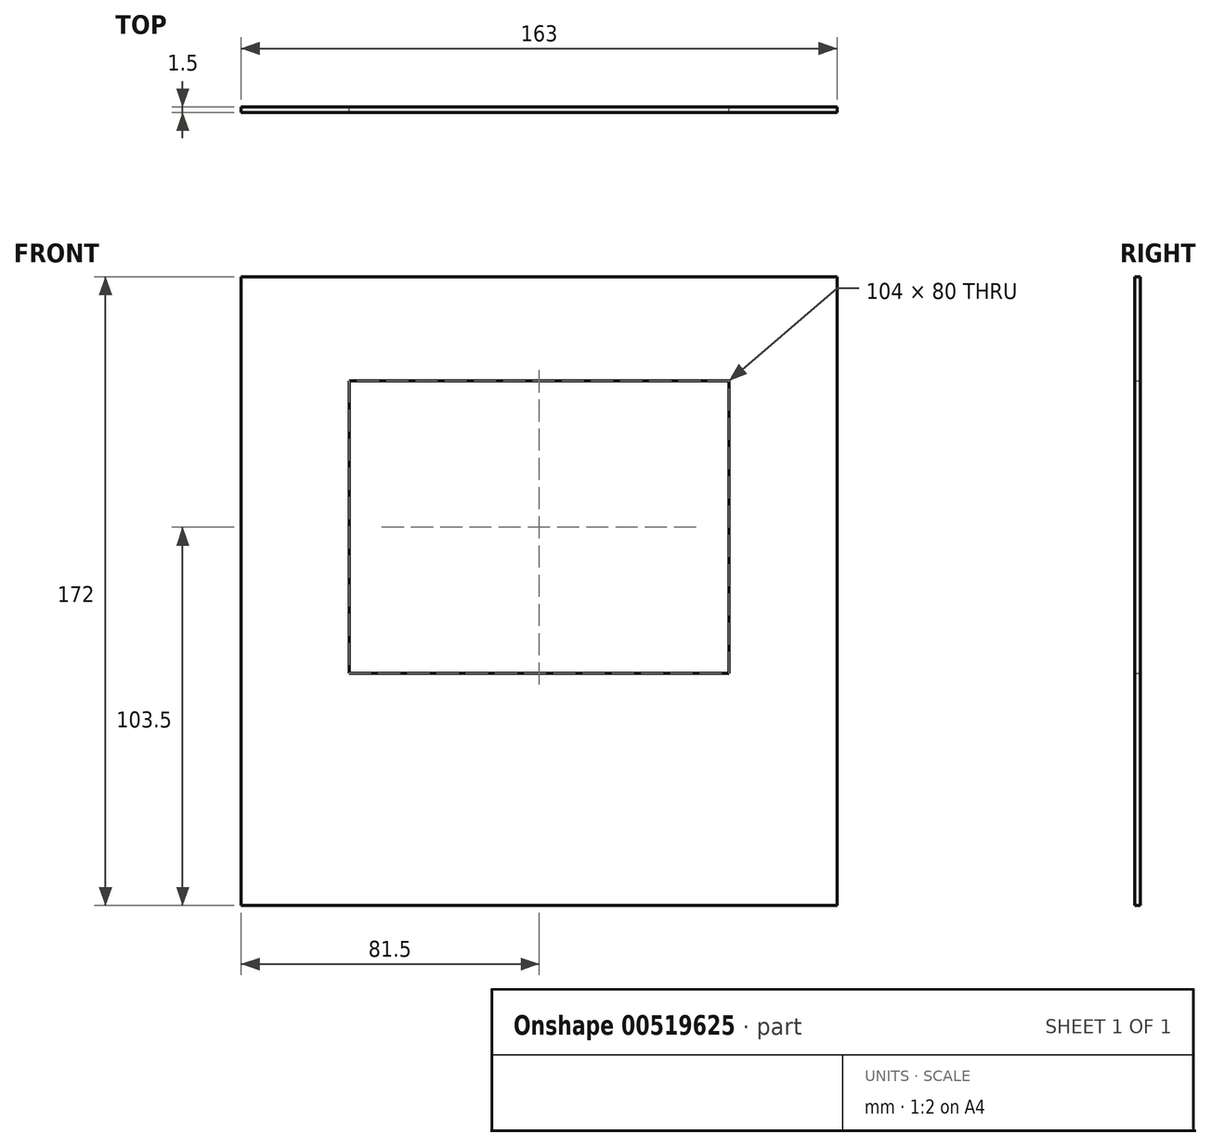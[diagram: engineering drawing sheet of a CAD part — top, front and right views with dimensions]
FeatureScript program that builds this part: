
annotation { "Feature Type Name" : "Feature", "Feature Type Description" : "" }
export const myFeature = defineFeature(function(context is Context, id is Id, definition is map)
    precondition{}
    {
        {
            var Q0;
            Q0=qCreatedBy(makeId("Front.planeOp"),FACE);
            var sketch = newSketch(context, id + "F0", { "sketchPlane" : qUnion([Q0])});
            skLineSegment(sketch, "E0.bottom", {"start": v(81.5, 86) * mm, "end": v(-81.5, 86) * mm});
            skLineSegment(sketch, "E0.top", {"start": v(81.5, -86) * mm, "end": v(3, -86) * mm});
            skLineSegment(sketch, "E0.left", {"start": v(81.5, 86) * mm, "end": v(81.5, -86) * mm});
            skLineSegment(sketch, "E0.right", {"start": v(-81.5, 86) * mm, "end": v(-81.5, -86) * mm});
            skPoint(sketch, "E0.middle", {"position": v(0, 0) * mm});
            skLineSegment(sketch, "E1.trimOffspring", {"start": v(-3, -86) * mm, "end": v(-81.5, -86) * mm});
            skLineSegment(sketch, "E2", {"start": v(3, -86) * mm, "end": v(-3, -86) * mm});
            skLineSegment(sketch, "E3.bottom", {"start": v(52, 57.5) * mm, "end": v(-52, 57.5) * mm});
            skLineSegment(sketch, "E3.top", {"start": v(52, -22.5) * mm, "end": v(-52, -22.5) * mm});
            skLineSegment(sketch, "E3.left", {"start": v(52, 57.5) * mm, "end": v(52, -22.5) * mm});
            skLineSegment(sketch, "E3.right", {"start": v(-52, 57.5) * mm, "end": v(-52, -22.5) * mm});
            skPoint(sketch, "E3.middle", {"position": v(0, 17.5) * mm});
            skSolve(sketch);
        }
        {
            var Q0;
            Q0=makeQuery(id+"F0.imprint","IMPRINT",FACE,{"disambiguationData":[TD([[makeQuery(id+"F0.imprint","IMPRINT",EDGE,{"derivedFrom":sQuery(id+"F0.wireOp",EDGE,"E0.bottom")}),1.0]])]});
            extrude(context, id + "F1", {"entities" : qUnion([Q0]), "depth" : 1.5 * mm, "offsetDistance" : 25 * mm});
        }
    });
